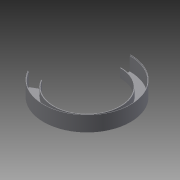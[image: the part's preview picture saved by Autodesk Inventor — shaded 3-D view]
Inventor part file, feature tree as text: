
AUTODESK INVENTOR PART (.ipt)
format: ipt  version: 2015 (Build 190159000, 159)  size: 103,936 bytes
history: native  units: in
note: dims shown in document units (in); Inventor stores cm internally (conversion verified against a paired STEP export)
features: revolve x1, sketch x1
ambient origin geometry x8: Origin, YZ Plane, XZ Plane, XY Plane, X Axis, Y Axis, Z Axis, Center Point
bodies: Solid1 (feature_tree)
feature tree (2):
  revolve  "Revolution1"  [1 undecoded]
  sketch  "Sketch1"  dims[d3=0.125in d10=1.45in d11=1.75in d12=2.5in d13=0.0625in d14=0.125in d15=0.0625in d16=0.125in d17=1.325in d18=1.5in d19=5.5in d20=2.2in d21=240.0deg]
note: 1 required parameter value undecoded (feature->parameter linkage not recoverable at this tier; creation-order binding heuristic only, values carry confidence <= 0.55)
